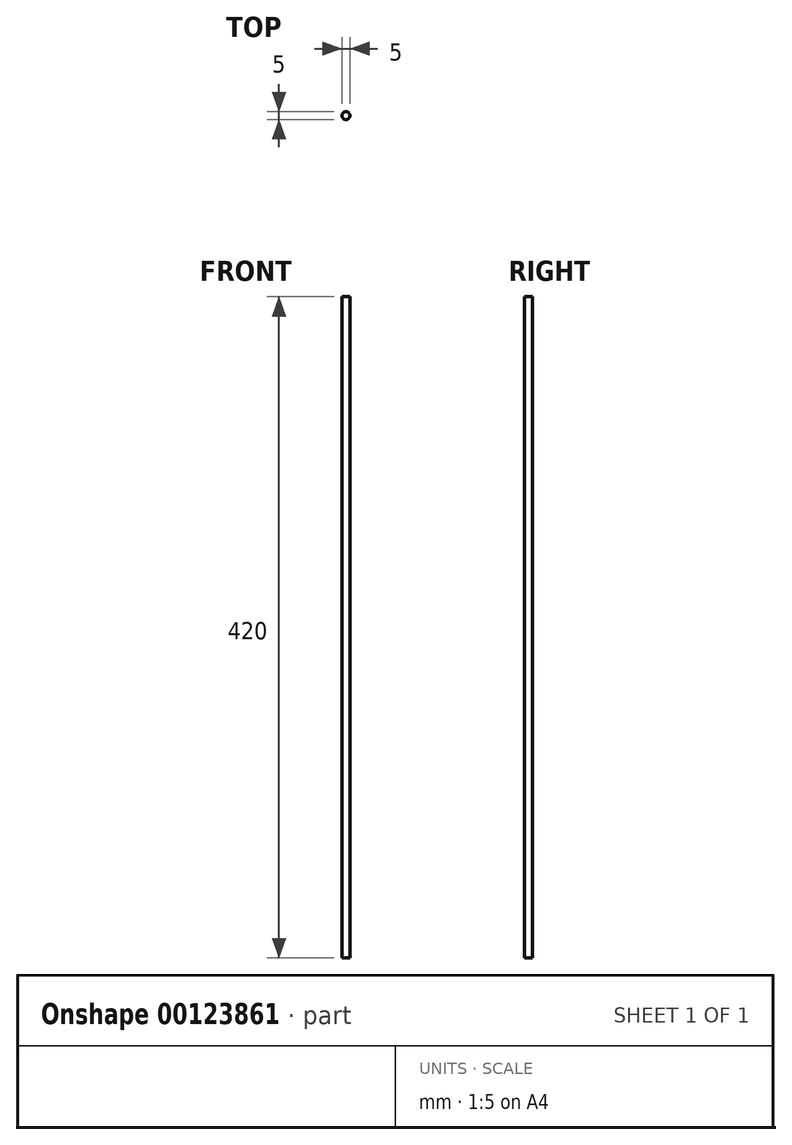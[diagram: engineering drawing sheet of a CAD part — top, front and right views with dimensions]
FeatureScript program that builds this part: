
annotation { "Feature Type Name" : "Feature", "Feature Type Description" : "" }
export const myFeature = defineFeature(function(context is Context, id is Id, definition is map)
    precondition{}
    {
        {
            var Q0;
            Q0=qCreatedBy(makeId("Top.planeOp"),FACE);
            var sketch = newSketch(context, id + "F0", { "sketchPlane" : qUnion([Q0])});
            skCircle(sketch, "E0", {"center": v(0, 0) * mm, "radius": 2.5 * mm});
            skSolve(sketch);
        }
        {
            var Q0;
            Q0=makeQuery(id+"F0.imprint","IMPRINT",FACE,{"disambiguationData":[TD([[makeQuery(id+"F0.imprint","IMPRINT",EDGE,{"derivedFrom":sQuery(id+"F0.wireOp",EDGE,"E0")}),1.0]])]});
            extrude(context, id + "F1", {"entities" : qUnion([Q0]), "depth" : 420 * mm});
        }
    });
